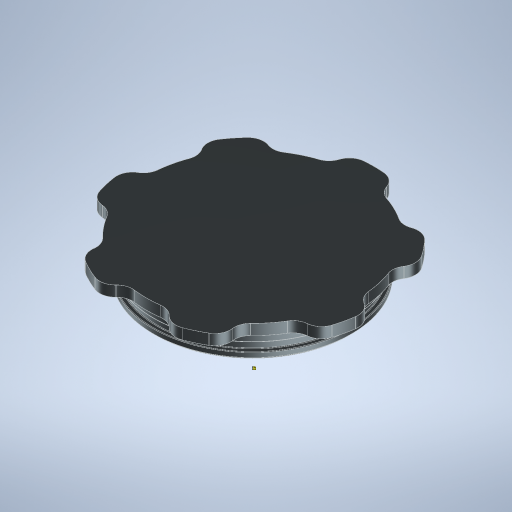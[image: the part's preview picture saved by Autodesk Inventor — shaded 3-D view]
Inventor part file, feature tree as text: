
AUTODESK INVENTOR PART (.ipt)
format: ipt  version: 2024.3 (Build 283343000, 343)  size: 371,200 bytes
history: native  units: mm
features: fillet x2, sketch x2, other x1, revolve x1, extrude x1, pattern_circular x1, chamfer x1
ambient origin geometry x8: Origin, YZ Plane, XZ Plane, XY Plane, X Axis, Y Axis, Z Axis, Center Point
bodies: Body1 (feature_tree)
feature tree (9):
  other  "Sólido1"
  revolve  "Revolución1"  [1 undecoded]
  extrude  "Extrusión2"  Depth=0.25mm
  fillet  "Empalme5"  Radius=0.275mm
  pattern_circular  "Patrón circular3"  [2 undecoded]
  fillet  "Empalme6"  Radius=3.7mm
  chamfer  "Chaflán1"  Angle=90.0deg  [1 undecoded]
  sketch  "Boceto1"  dims[d1=5.0mm d4=0.0mm]
  sketch  "Boceto6"  dims[d6=0.872665mm d7=94.0mm d9=0.275mm d10=2.1mm d11=3.7mm d12=90.0deg d14=89.8mm d88=20.0mm d89=4.363323mm d90=7.5mm d91=10.0mm d92=0.0mm d93=7.5mm d94=70.0mm d95=360.0deg d98=0.25mm d99=1.0mm d100=2.0mm d101=45.0deg]
note: 4 required parameter values undecoded (feature->parameter linkage not recoverable at this tier; creation-order binding heuristic only, values carry confidence <= 0.55)